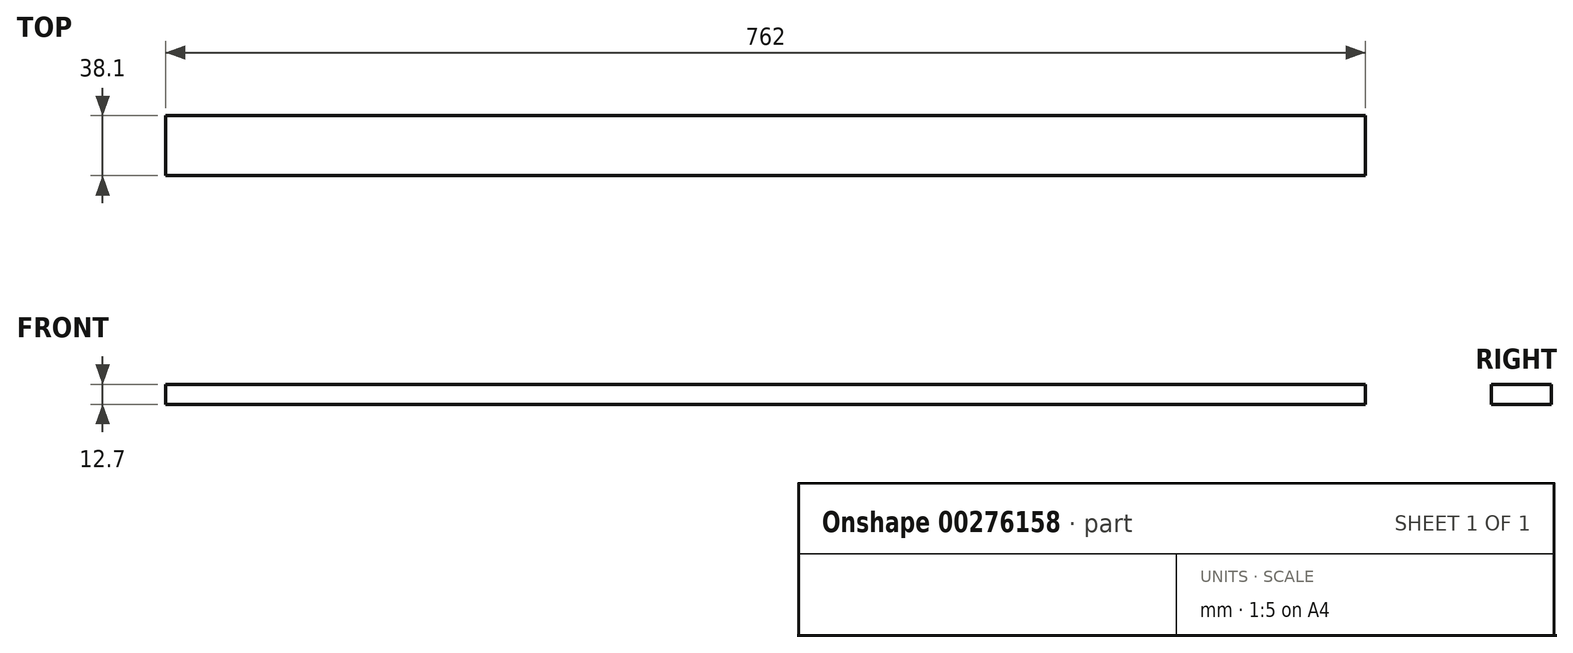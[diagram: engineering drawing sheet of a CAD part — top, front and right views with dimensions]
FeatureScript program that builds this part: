
annotation { "Feature Type Name" : "Feature", "Feature Type Description" : "" }
export const myFeature = defineFeature(function(context is Context, id is Id, definition is map)
    precondition{}
    {
        {
            var Q0;
            Q0=qCreatedBy(makeId("Right.planeOp"),FACE);
            var sketch = newSketch(context, id + "F0", { "sketchPlane" : qUnion([Q0])});
            skLineSegment(sketch, "E0.bottom", {"start": v(0, 0) * mm, "end": v(38.1, 0) * mm});
            skLineSegment(sketch, "E0.top", {"start": v(0, 12.7) * mm, "end": v(38.1, 12.7) * mm});
            skLineSegment(sketch, "E0.left", {"start": v(0, 0) * mm, "end": v(0, 12.7) * mm});
            skLineSegment(sketch, "E0.right", {"start": v(38.1, 0) * mm, "end": v(38.1, 12.7) * mm});
            skSolve(sketch);
        }
        {
            var Q0;
            Q0=makeQuery(id+"F0.imprint","IMPRINT",FACE,{"disambiguationData":[TD([[makeQuery(id+"F0.imprint","IMPRINT",EDGE,{"derivedFrom":sQuery(id+"F0.wireOp",EDGE,"E0.bottom")}),1.0]])]});
            extrude(context, id + "F1", {"entities" : qUnion([Q0]), "oppositeDirection" : true, "depth" : 762 * mm});
        }
    });
